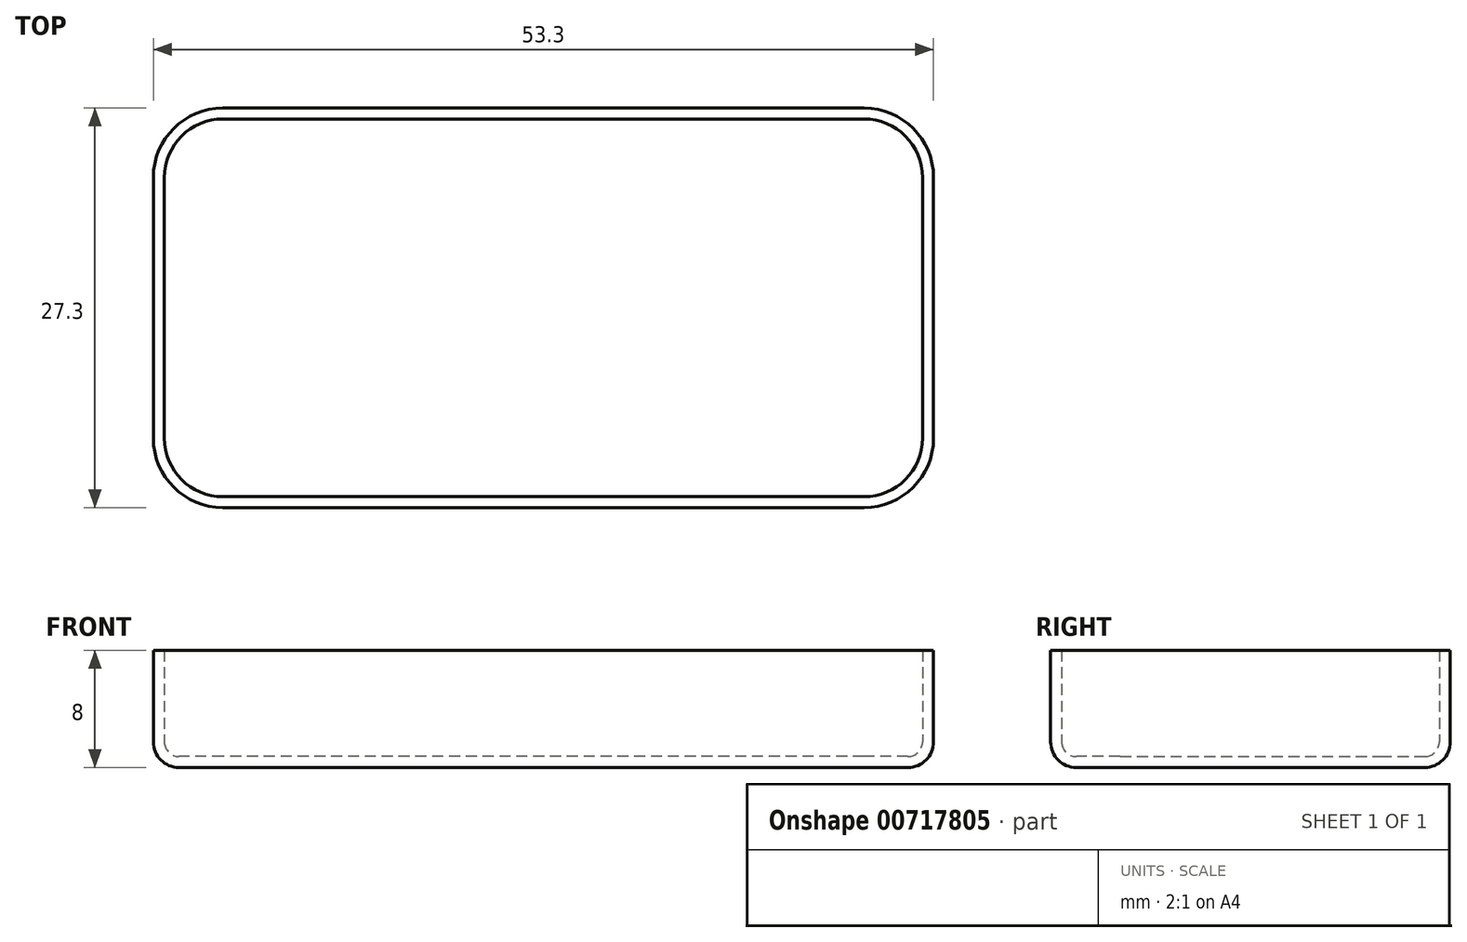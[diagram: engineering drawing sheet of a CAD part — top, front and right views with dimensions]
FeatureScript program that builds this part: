
annotation { "Feature Type Name" : "Feature", "Feature Type Description" : "" }
export const myFeature = defineFeature(function(context is Context, id is Id, definition is map)
    precondition{}
    {
        {
            var Q0;
            Q0=qCreatedBy(makeId("Top.planeOp"),FACE);
            var sketch = newSketch(context, id + "F0", { "sketchPlane" : qUnion([Q0])});
            skLineSegment(sketch, "E0.bottom", {"start": v(26.65, -13.65) * mm, "end": v(-26.65, -13.65) * mm});
            skLineSegment(sketch, "E0.top", {"start": v(26.65, 13.65) * mm, "end": v(-26.65, 13.65) * mm});
            skLineSegment(sketch, "E0.left", {"start": v(26.65, -13.65) * mm, "end": v(26.65, 13.65) * mm});
            skLineSegment(sketch, "E0.right", {"start": v(-26.65, -13.65) * mm, "end": v(-26.65, 13.65) * mm});
            skPoint(sketch, "E0.middle", {"position": v(0, 0) * mm});
            skLineSegment(sketch, "E1.bottom", {"start": v(-25.9, 12.9) * mm, "end": v(25.9, 12.9) * mm});
            skLineSegment(sketch, "E1.top", {"start": v(-25.9, -12.9) * mm, "end": v(25.9, -12.9) * mm});
            skLineSegment(sketch, "E1.left", {"start": v(-25.9, 12.9) * mm, "end": v(-25.9, -12.9) * mm});
            skLineSegment(sketch, "E1.right", {"start": v(25.9, 12.9) * mm, "end": v(25.9, -12.9) * mm});
            skSolve(sketch);
        }
        {
            var Q0;
            Q0 = qSketchRegion(id + "F0", true);
            var Q1;
            Q1=makeQuery(id+"F0.imprint","IMPRINT",FACE,{"disambiguationData":[TD([[makeQuery(id+"F0.imprint","IMPRINT",EDGE,{"derivedFrom":sQuery(id+"F0.wireOp",EDGE,"E1.bottom")}),-1.0]])]});
            extrude(context, id + "F1", {"entities" : qUnion([Q0, Q1]), "depth" : .75 * mm, "offsetDistance" : 25 * mm});
        }
        {
            var Q0;
            Q0=makeQuery(id+"F0.imprint","IMPRINT",FACE,{"disambiguationData":[TD([[makeQuery(id+"F0.imprint","IMPRINT",EDGE,{"derivedFrom":sQuery(id+"F0.wireOp",EDGE,"E0.bottom")}),-1.0]])]});
            extrude(context, id + "F2", {"entities" : qUnion([Q0]), "operationType" : NewBodyOperationType.ADD, "depth" : 8 * mm, "offsetDistance" : 25 * mm});
        }
        {
            var Q0;
            Q0=makeQuery(id+"F2.opExtrude","SWEPT_EDGE",EDGE,{"disambiguationData":[OSD([sQuery(id+"F0.wireOp",EDGE,"E1.bottom"),sQuery(id+"F0.wireOp",EDGE,"E1.left")])]});
            var Q1;
            Q1=makeQuery(id+"F2.opExtrude","SWEPT_EDGE",EDGE,{"disambiguationData":[OSD([sQuery(id+"F0.wireOp",EDGE,"E1.bottom"),sQuery(id+"F0.wireOp",EDGE,"E1.right")])]});
            var Q2;
            Q2=makeQuery(id+"F2.opExtrude","SWEPT_EDGE",EDGE,{"disambiguationData":[OSD([sQuery(id+"F0.wireOp",EDGE,"E1.top"),sQuery(id+"F0.wireOp",EDGE,"E1.right")])]});
            var Q3;
            Q3=makeQuery(id+"F2.opExtrude","SWEPT_EDGE",EDGE,{"disambiguationData":[OSD([sQuery(id+"F0.wireOp",EDGE,"E1.top"),sQuery(id+"F0.wireOp",EDGE,"E1.left")])]});
            fillet(context, id + "F3", {"entities" : qUnion([Q0, Q1, Q2, Q3]), "radius" : 4 * mm, "tangentPropagation" : true, "allowEdgeOverflow" : false});
        }
        {
            var Q0;
            {var subQ0=sQuery(id+"F0.wireOp",EDGE,"E0.left");var subQ1=sQuery(id+"F0.wireOp",EDGE,"E0.top");Q0=makeQuery(id+"F2.boolean.opBoolean","MERGE",EDGE,{"derivedFrom":[makeQuery(id+"F1.opExtrude","SWEPT_EDGE",EDGE,{"disambiguationData":[OSD([subQ1,subQ0])]}),makeQuery(id+"F2.opExtrude","SWEPT_EDGE",EDGE,{"disambiguationData":[OSD([subQ1,subQ0])]})]});}
            var Q1;
            {var subQ0=sQuery(id+"F0.wireOp",EDGE,"E0.left");var subQ1=sQuery(id+"F0.wireOp",EDGE,"E0.bottom");Q1=makeQuery(id+"F2.boolean.opBoolean","MERGE",EDGE,{"derivedFrom":[makeQuery(id+"F1.opExtrude","SWEPT_EDGE",EDGE,{"disambiguationData":[OSD([subQ1,subQ0])]}),makeQuery(id+"F2.opExtrude","SWEPT_EDGE",EDGE,{"disambiguationData":[OSD([subQ1,subQ0])]})]});}
            var Q2;
            {var subQ0=sQuery(id+"F0.wireOp",EDGE,"E0.right");var subQ1=sQuery(id+"F0.wireOp",EDGE,"E0.top");Q2=makeQuery(id+"F2.boolean.opBoolean","MERGE",EDGE,{"derivedFrom":[makeQuery(id+"F1.opExtrude","SWEPT_EDGE",EDGE,{"disambiguationData":[OSD([subQ1,subQ0])]}),makeQuery(id+"F2.opExtrude","SWEPT_EDGE",EDGE,{"disambiguationData":[OSD([subQ1,subQ0])]})]});}
            var Q3;
            {var subQ0=sQuery(id+"F0.wireOp",EDGE,"E0.right");var subQ1=sQuery(id+"F0.wireOp",EDGE,"E0.bottom");Q3=makeQuery(id+"F2.boolean.opBoolean","MERGE",EDGE,{"derivedFrom":[makeQuery(id+"F1.opExtrude","SWEPT_EDGE",EDGE,{"disambiguationData":[OSD([subQ1,subQ0])]}),makeQuery(id+"F2.opExtrude","SWEPT_EDGE",EDGE,{"disambiguationData":[OSD([subQ1,subQ0])]})]});}
            fillet(context, id + "F4", {"entities" : qUnion([Q0, Q1, Q2, Q3]), "radius" : 4.75 * mm, "tangentPropagation" : true, "allowEdgeOverflow" : false});
        }
        {
            var Q0;
            Q0=makeQuery(id+"F2.boolean.opBoolean","INTERSECT",EDGE,{"derivedFrom":[makeQuery(id+"F1.opExtrude","CAP_FACE",FACE,{"disambiguationData":[OSD([sQuery(id+"F0.wireOp",EDGE,"E0.bottom"),sQuery(id+"F0.wireOp",EDGE,"E0.top"),sQuery(id+"F0.wireOp",EDGE,"E0.left"),sQuery(id+"F0.wireOp",EDGE,"E0.right")])],"isStart":false}),makeQuery(id+"F2.opExtrude","SWEPT_FACE",FACE,{"disambiguationData":[OSD([sQuery(id+"F0.wireOp",EDGE,"E1.bottom")])]})]});
            fillet(context, id + "F5", {"entities" : qUnion([Q0]), "radius" : 1 * mm, "tangentPropagation" : true, "allowEdgeOverflow" : false});
        }
        {
            var Q0;
            Q0=makeQuery(id+"F1.opExtrude","CAP_EDGE",EDGE,{"disambiguationData":[OSD([sQuery(id+"F0.wireOp",EDGE,"E0.top")])],"isStart":true});
            fillet(context, id + "F6", {"entities" : qUnion([Q0]), "radius" : 1.75 * mm, "tangentPropagation" : true, "allowEdgeOverflow" : false});
        }
    });
